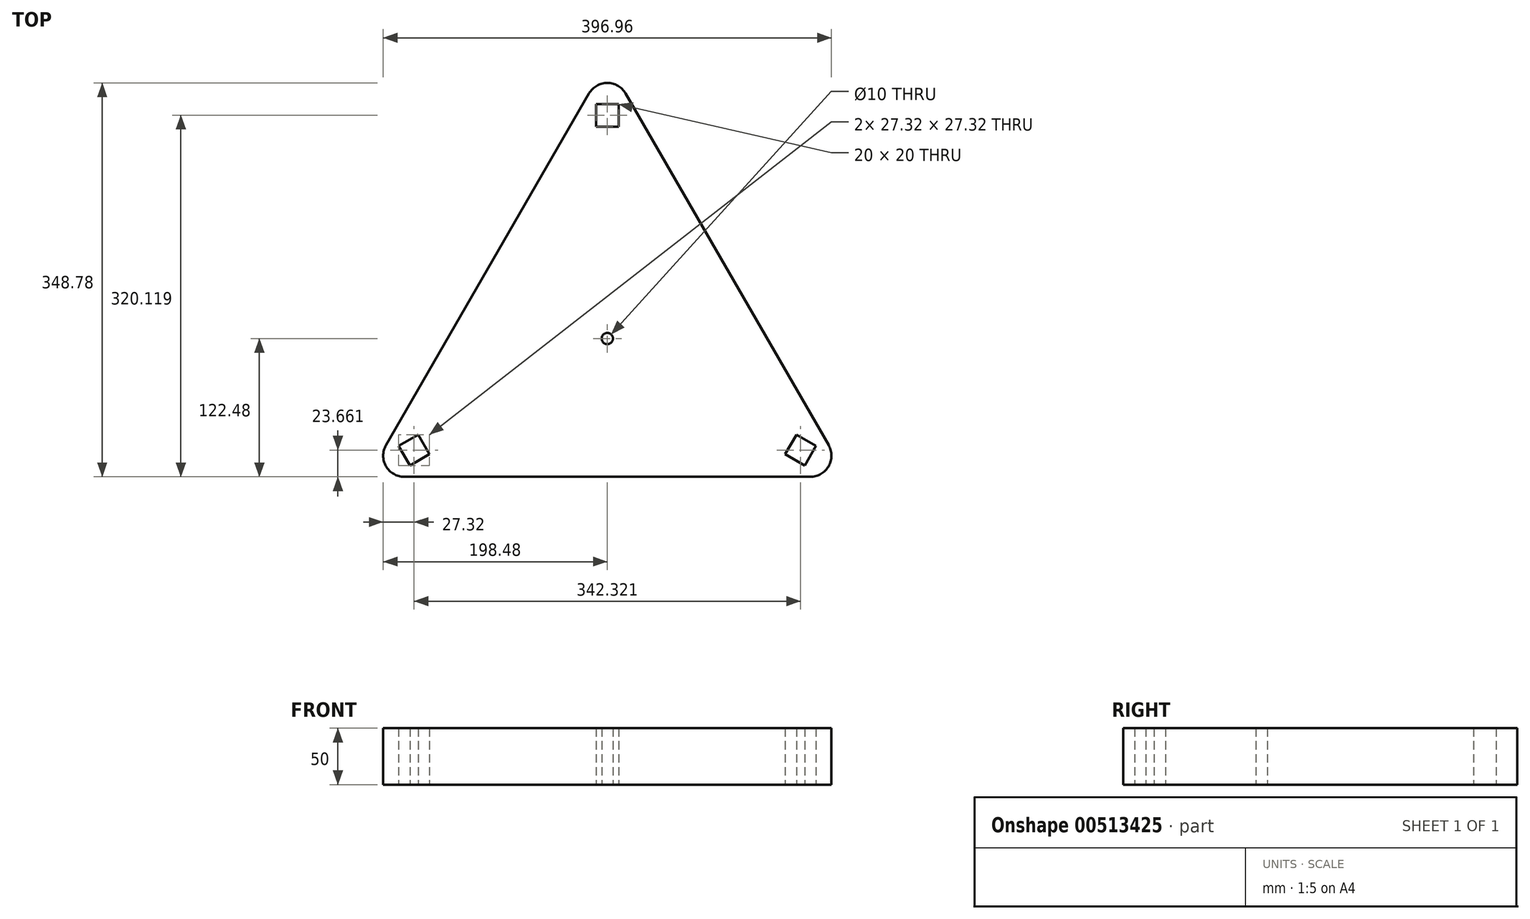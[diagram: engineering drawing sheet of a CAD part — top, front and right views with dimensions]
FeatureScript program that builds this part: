
annotation { "Feature Type Name" : "Feature", "Feature Type Description" : "" }
export const myFeature = defineFeature(function(context is Context, id is Id, definition is map)
    precondition{}
    {
        {
            var Q0;
            Q0=qCreatedBy(makeId("Top.planeOp"),FACE);
            var sketch = newSketch(context, id + "F0", { "sketchPlane" : qUnion([Q0])});
            skCircle(sketch, "E0", {"center": v(0, 0) * mm, "radius": 187.64 * mm, "construction": true});
            skLineSegment(sketch, "E1.bottom", {"start": v(-10, 207.64) * mm, "end": v(10, 207.64) * mm});
            skLineSegment(sketch, "E1.top", {"start": v(-10, 187.64) * mm, "end": v(10, 187.64) * mm});
            skLineSegment(sketch, "E1.left", {"start": v(-10, 207.64) * mm, "end": v(-10, 187.64) * mm});
            skLineSegment(sketch, "E1.right", {"start": v(10, 207.64) * mm, "end": v(10, 187.64) * mm});
            skLineSegment(sketch, "E2", {"start": v(0, 187.64) * mm, "end": v(0, 0) * mm, "construction": true});
            skLineSegment(sketch, "E3.1.0", {"start": v(-157.5, -102.48) * mm, "end": v(-167.5, -85.16) * mm});
            skLineSegment(sketch, "E3.1.1", {"start": v(-174.82, -112.48) * mm, "end": v(-184.82, -95.16) * mm});
            skLineSegment(sketch, "E3.1.2", {"start": v(-184.82, -95.16) * mm, "end": v(-167.5, -85.16) * mm});
            skLineSegment(sketch, "E3.1.3", {"start": v(-174.82, -112.48) * mm, "end": v(-157.5, -102.48) * mm});
            skLineSegment(sketch, "E3.1.4", {"start": v(-162.5, -93.82) * mm, "end": v(0, 0) * mm, "construction": true});
            skLineSegment(sketch, "E3.2.0", {"start": v(167.5, -85.16) * mm, "end": v(157.5, -102.48) * mm});
            skLineSegment(sketch, "E3.2.1", {"start": v(184.82, -95.16) * mm, "end": v(174.82, -112.48) * mm});
            skLineSegment(sketch, "E3.2.2", {"start": v(174.82, -112.48) * mm, "end": v(157.5, -102.48) * mm});
            skLineSegment(sketch, "E3.2.3", {"start": v(184.82, -95.16) * mm, "end": v(167.5, -85.16) * mm});
            skLineSegment(sketch, "E3.2.4", {"start": v(162.5, -93.82) * mm, "end": v(0, 0) * mm, "construction": true});
            skLineSegment(sketch, "E4", {"start": v(-184.82, -95.16) * mm, "end": v(-10, 207.64) * mm, "construction": true});
            skLineSegment(sketch, "E5", {"start": v(10, 207.64) * mm, "end": v(184.82, -95.16) * mm, "construction": true});
            skLineSegment(sketch, "E6", {"start": v(174.82, -112.48) * mm, "end": v(-174.82, -112.48) * mm, "construction": true});
            skLineSegment(sketch, "E7.0", {"start": v(-195.98, -94.49) * mm, "end": v(-16.16, 216.97) * mm});
            skLineSegment(sketch, "E8.0", {"start": v(16.16, 216.97) * mm, "end": v(195.98, -94.49) * mm});
            skLineSegment(sketch, "E9.0", {"start": v(179.82, -122.48) * mm, "end": v(-179.82, -122.48) * mm});
            skArc(sketch, "E10", {"start": v(-195.98, -94.49) * mm, "mid": v(-195.98, -113.15) * mm, "end": v(-179.82, -122.48) * mm});
            skArc(sketch, "E11", {"start": v(195.98, -94.49) * mm, "mid": v(195.98, -113.15) * mm, "end": v(179.82, -122.48) * mm});
            skArc(sketch, "E12", {"start": v(-16.16, 216.97) * mm, "mid": v(0, 226.3) * mm, "end": v(16.16, 216.97) * mm});
            skCircle(sketch, "E13", {"center": v(0, 0) * mm, "radius": 5 * mm});
            skSolve(sketch);
        }
        {
            var Q0;
            Q0=makeQuery(id+"F0.imprint","IMPRINT",FACE,{"disambiguationData":[TD([[makeQuery(id+"F0.imprint","IMPRINT",EDGE,{"derivedFrom":sQuery(id+"F0.wireOp",EDGE,"E1.bottom")}),1.0]])]});
            extrude(context, id + "F1", {"entities" : qUnion([Q0]), "depth" : 50 * mm});
        }
    });
